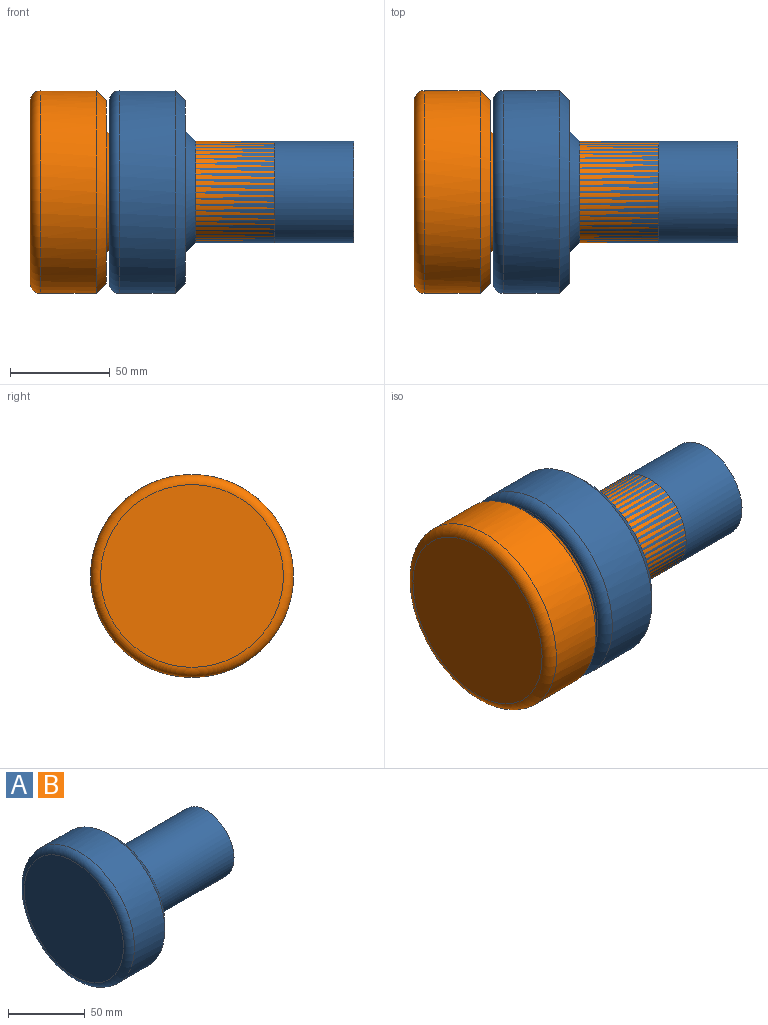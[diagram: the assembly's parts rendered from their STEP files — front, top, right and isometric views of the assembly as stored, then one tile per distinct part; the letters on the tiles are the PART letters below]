
ASSEMBLY  parts=2 mates=1
PART A: 10 faces, bbox 122.3x110x110 mm
  f0: plane 91.44x91.44mm, normal (-1,0,0), area 6566.9mm2, adj f7
  f1: cylinder r=25.4mm len=79.1mm, axis (1,0,0), area 12623.7mm2, adj f4,f8
  f2: plane 91.44x91.44mm, normal (1,0,0), area 3648.3mm2, adj f8,f9
  f3: cylinder r=50.8mm len=101.6mm, axis (1,0,0), area 8918.1mm2, adj f7,f9
  f4: plane 50.8x50.8mm, normal (1,0,0), area 1778.5mm2, adj f1,f6
  f5: cone r=0mm half-angle=59deg, axis (1,0,0), area 289.7mm2, adj f6
  f6: cylinder r=8.89mm len=17.78mm, axis (1,0,0), area 709.4mm2, adj f4,f5
  f7: torus R=45.72mm, axis (1,0,0), area 2454.4mm2, adj f0,f3
  f8: cone r=25.4mm half-angle=45deg, axis (-1,0,0), area 1261.2mm2, adj f1,f2
  f9: cone r=45.72mm half-angle=45deg, axis (-1,0,0), area 2178.4mm2, adj f2,f3
PART B: same geometry as A
PLACE A t=(127.43,63.23,-34.21)mm
PLACE B t=(87.88,63.23,-34.21)mm
MATE revolute A.f1 <-> B.f1  axis (1,0,0) through (170.61,63.23,-34.21)mm
